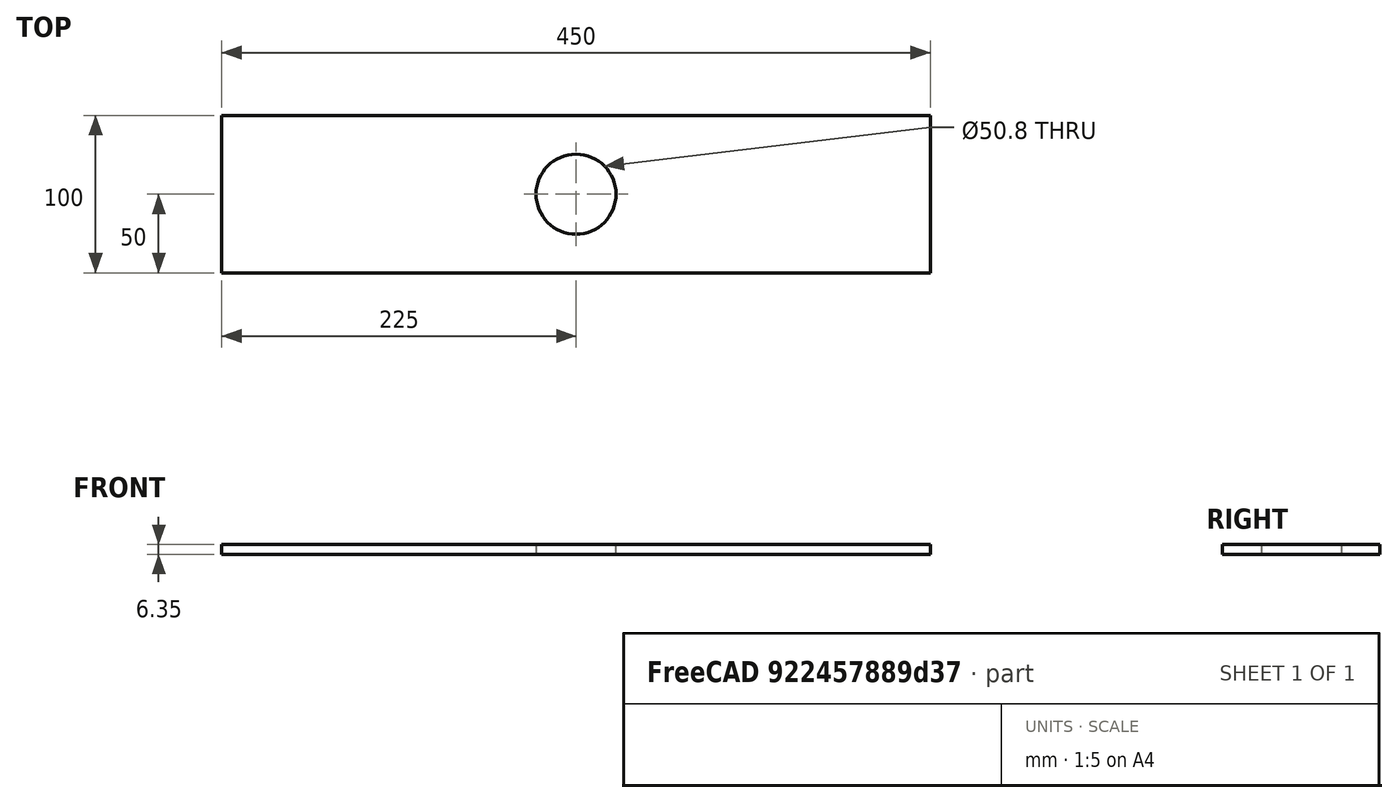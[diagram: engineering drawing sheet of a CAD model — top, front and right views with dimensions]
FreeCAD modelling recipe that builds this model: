
FCSTD DOCUMENT  (FreeCAD 0.16RUnknown)
Label: Lateral con entrada
License: All rights reserved
LicenseURL: http://berserk.design
objects: Sketcher::SketchObject×1, PartDesign::Pad×1
note: 3 computed .brp shape members not serialized (recipe doc carries the construction recipe); baked Part::Feature solids carry a one-line shape summary decoded from their .brp

FEATURE [Sketcher::SketchObject] Sketch
  sketch-geometry (7):
    g0: LineSegment StartX=0 StartY=0 StartZ=0 EndX=450 EndY=0 EndZ=0
    g1: LineSegment StartX=450 StartY=0 StartZ=0 EndX=450 EndY=100 EndZ=0
    g2: LineSegment StartX=450 StartY=100 StartZ=0 EndX=0 EndY=100 EndZ=0
    g3: LineSegment StartX=0 StartY=100 StartZ=0 EndX=0 EndY=0 EndZ=0
    g4: Circle CenterX=225 CenterY=50 CenterZ=0 NormalX=0 NormalY=0 NormalZ=1 Radius=25.4
    g5: LineSegment [constr] StartX=225 StartY=50 StartZ=0 EndX=225 EndY=100 EndZ=0
    g6: LineSegment [constr] StartX=225 StartY=50 StartZ=0 EndX=450 EndY=50 EndZ=0
  constraints (20):
    c: Coincident(g0,g1)
    c: Coincident(g1,g2)
    c: Coincident(g2,g3)
    c: Coincident(g3,g0)
    c: Horizontal(g0)
    c: Horizontal(g2)
    c: Vertical(g1)
    c: Vertical(g3)
    c: Coincident(g0,g-1)
    c: DistanceX(g2,g2) = 450
    c: DistanceY(g3,g3) = 100
    c: Coincident(g5,g4)
    c: PointOnObject(g5,g2)
    c: Vertical(g5)
    c: Radius(g4) = 25.4
    c: Symmetric(g2,g1,g5)
    c: Coincident(g6,g4)
    c: PointOnObject(g6,g1)
    c: Horizontal(g6)
    c: Symmetric(g0,g1,g6)
FEATURE [PartDesign::Pad] Pad
  Length = 6.35
  Length2 = 100
  Sketch = -> Sketch
  Type = 0
